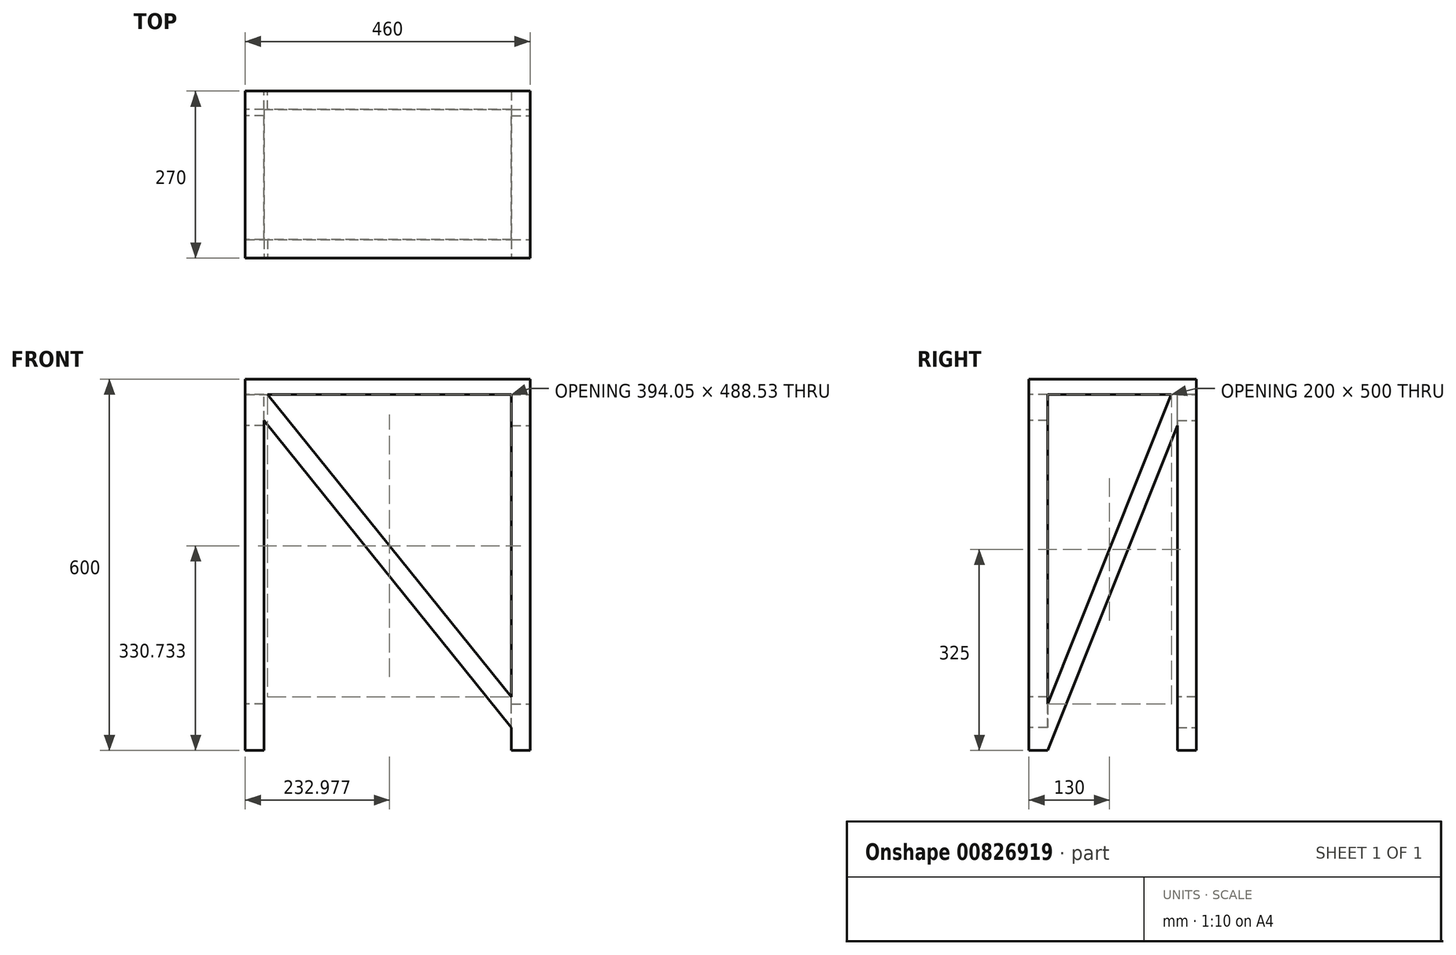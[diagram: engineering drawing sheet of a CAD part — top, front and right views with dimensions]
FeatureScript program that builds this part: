
annotation { "Feature Type Name" : "Feature", "Feature Type Description" : "" }
export const myFeature = defineFeature(function(context is Context, id is Id, definition is map)
    precondition{}
    {
        {
            var Q0;
            Q0=qCreatedBy(makeId("Top.planeOp"),FACE);
            var sketch = newSketch(context, id + "F0", { "sketchPlane" : qUnion([Q0])});
            skLineSegment(sketch, "E0.bottom", {"start": v(-200, 105) * mm, "end": v(-230, 105) * mm});
            skLineSegment(sketch, "E0.top", {"start": v(-200, 135) * mm, "end": v(-230, 135) * mm});
            skLineSegment(sketch, "E0.left", {"start": v(-200, 105) * mm, "end": v(-200, 135) * mm});
            skLineSegment(sketch, "E0.right", {"start": v(-230, 105) * mm, "end": v(-230, 135) * mm});
            skPoint(sketch, "E0.middle", {"position": v(-215, 120) * mm});
            skLineSegment(sketch, "E1.0.1.0", {"start": v(-200, -135) * mm, "end": v(-200, -105) * mm});
            skLineSegment(sketch, "E1.0.1.1", {"start": v(-230, -135) * mm, "end": v(-230, -105) * mm});
            skLineSegment(sketch, "E1.0.1.2", {"start": v(-200, -135) * mm, "end": v(-230, -135) * mm});
            skLineSegment(sketch, "E1.0.1.3", {"start": v(-200, -105) * mm, "end": v(-230, -105) * mm});
            skPoint(sketch, "E1.0.1.4", {"position": v(-215, -120) * mm});
            skLineSegment(sketch, "E1.1.0.0", {"start": v(230, 105) * mm, "end": v(230, 135) * mm});
            skLineSegment(sketch, "E1.1.0.1", {"start": v(200, 105) * mm, "end": v(200, 135) * mm});
            skLineSegment(sketch, "E1.1.0.2", {"start": v(230, 105) * mm, "end": v(200, 105) * mm});
            skLineSegment(sketch, "E1.1.0.3", {"start": v(230, 135) * mm, "end": v(200, 135) * mm});
            skPoint(sketch, "E1.1.0.4", {"position": v(215, 120) * mm});
            skLineSegment(sketch, "E1.1.1.0", {"start": v(230, -135) * mm, "end": v(230, -105) * mm});
            skLineSegment(sketch, "E1.1.1.1", {"start": v(200, -135) * mm, "end": v(200, -105) * mm});
            skLineSegment(sketch, "E1.1.1.2", {"start": v(230, -135) * mm, "end": v(200, -135) * mm});
            skLineSegment(sketch, "E1.1.1.3", {"start": v(230, -105) * mm, "end": v(200, -105) * mm});
            skPoint(sketch, "E1.1.1.4", {"position": v(215, -120) * mm});
            skLineSegment(sketch, "E1.direction1", {"start": v(-230, 105) * mm, "end": v(200, 105) * mm, "construction": true});
            skLineSegment(sketch, "E1.direction2", {"start": v(-230, 105) * mm, "end": v(-230, -135) * mm, "construction": true});
            skSolve(sketch);
        }
        {
            var Q0;
            Q0 = qSketchRegion(id + "F0", true);
            extrude(context, id + "F1", {"entities" : qUnion([Q0]), "oppositeDirection" : true, "depth" : 600 * mm, "offsetDistance" : 25 * mm});
        }
        {
            var Q0;
            Q0=makeQuery(id+"F1.opExtrude","CAP_FACE",FACE,{"disambiguationData":[OSD([sQuery(id+"F0.wireOp",EDGE,"E0.bottom"),sQuery(id+"F0.wireOp",EDGE,"E0.top"),sQuery(id+"F0.wireOp",EDGE,"E0.left"),sQuery(id+"F0.wireOp",EDGE,"E0.right")])],"isStart":true});
            var sketch = newSketch(context, id + "F2", { "sketchPlane" : qUnion([Q0])});
            skLineSegment(sketch, "E2.bottom", {"start": v(-230, 135) * mm, "end": v(230, 135) * mm});
            skLineSegment(sketch, "E2.top", {"start": v(-230, -135) * mm, "end": v(230, -135) * mm});
            skLineSegment(sketch, "E2.left", {"start": v(-230, 135) * mm, "end": v(-230, -135) * mm});
            skLineSegment(sketch, "E2.right", {"start": v(230, 135) * mm, "end": v(230, -135) * mm});
            skSolve(sketch);
        }
        {
            var Q0;
            Q0 = qSketchRegion(id + "F2", true);
            extrude(context, id + "F3", {"entities" : qUnion([Q0]), "operationType" : NewBodyOperationType.ADD, "oppositeDirection" : true, "depth" : 25 * mm, "offsetDistance" : 25 * mm});
        }
        {
            var Q0;
            Q0=makeQuery(id+"F3.boolean.opBoolean","MERGE",FACE,{"derivedFrom":[makeQuery(id+"F1.opExtrude","SWEPT_FACE",FACE,{"disambiguationData":[OSD([sQuery(id+"F0.wireOp",EDGE,"E1.0.1.2")])]}),makeQuery(id+"F1.opExtrude","SWEPT_FACE",FACE,{"disambiguationData":[OSD([sQuery(id+"F0.wireOp",EDGE,"E1.1.1.2")])]}),makeQuery(id+"F3.opExtrude","SWEPT_FACE",FACE,{"disambiguationData":[OSD([sQuery(id+"F2.wireOp",EDGE,"E2.top")])]})]});
            var sketch = newSketch(context, id + "F4", { "sketchPlane" : qUnion([Q0])});
            skLineSegment(sketch, "E3", {"start": v(-230, -29.7) * mm, "end": v(230, -600) * mm});
            skLineSegment(sketch, "E4", {"start": v(230, -600) * mm, "end": v(230, -550.73) * mm});
            skLineSegment(sketch, "E5", {"start": v(230, -550.73) * mm, "end": v(-214.2, 0) * mm});
            skLineSegment(sketch, "E6", {"start": v(-214.2, 0) * mm, "end": v(-230, -29.7) * mm});
            skSolve(sketch);
        }
        {
            var Q0;
            {var subQ3=sQuery(id+"F4.wireOp",EDGE,"E5");var subQ5=makeQuery(id+"F3.opExtrude","CAP_EDGE",EDGE,{"disambiguationData":[OSD([sQuery(id+"F2.wireOp",EDGE,"E2.top")])],"isStart":false});var subQ9=makeQuery(id+"F4.imprint","INTERSECT",VERTEX,{"derivedFrom":[subQ5,subQ3]});Q0=makeQuery(id+"F4.imprint","IMPRINT",FACE,{"disambiguationData":[TD([[makeQuery(id+"F4.imprint","IMPRINT",EDGE,{"disambiguationData":[TD([[subQ9,1.0]])],"derivedFrom":subQ3}),1.0]])]});}
            extrude(context, id + "F5", {"entities" : qUnion([Q0]), "operationType" : NewBodyOperationType.ADD, "oppositeDirection" : true, "depth" : 30 * mm, "offsetDistance" : 25 * mm});
        }
        {
            var Q0;
            Q0=makeQuery(id+"F1.opExtrude","SWEPT_FACE",FACE,{"disambiguationData":[OSD([sQuery(id+"F0.wireOp",EDGE,"E0.bottom")])]});
            var sketch = newSketch(context, id + "F6", { "sketchPlane" : qUnion([Q0])});
            skLineSegment(sketch, "E7.0", {"start": v(-230, -29.7) * mm, "end": v(230, -600) * mm});
            skLineSegment(sketch, "E8.0", {"start": v(230, -550.73) * mm, "end": v(-214.2, 0) * mm});
            skLineSegment(sketch, "E9.0", {"start": v(-214.2, 0) * mm, "end": v(-230, -29.7) * mm});
            skLineSegment(sketch, "E10.0", {"start": v(230, -600) * mm, "end": v(230, -550.73) * mm});
            skSolve(sketch);
        }
        {
            var Q0;
            Q0 = qSketchRegion(id + "F6", true);
            extrude(context, id + "F7", {"entities" : qUnion([Q0]), "operationType" : NewBodyOperationType.ADD, "oppositeDirection" : true, "depth" : 30 * mm, "offsetDistance" : 25 * mm});
        }
        {
            var Q0;
            Q0=makeQuery(id+"F3.boolean.opBoolean","MERGE",FACE,{"derivedFrom":[makeQuery(id+"F1.opExtrude","SWEPT_FACE",FACE,{"disambiguationData":[OSD([sQuery(id+"F0.wireOp",EDGE,"E0.right")])]}),makeQuery(id+"F1.opExtrude","SWEPT_FACE",FACE,{"disambiguationData":[OSD([sQuery(id+"F0.wireOp",EDGE,"E1.0.1.1")])]}),makeQuery(id+"F3.opExtrude","SWEPT_FACE",FACE,{"disambiguationData":[OSD([sQuery(id+"F2.wireOp",EDGE,"E2.left")])]})]});
            var sketch = newSketch(context, id + "F8", { "sketchPlane" : qUnion([Q0])});
            skLineSegment(sketch, "E11", {"start": v(-135, 0) * mm, "end": v(105, -600) * mm});
            skLineSegment(sketch, "E12", {"start": v(105, -600) * mm, "end": v(135, -600) * mm});
            skLineSegment(sketch, "E13", {"start": v(135, -600) * mm, "end": v(-105, 0) * mm});
            skLineSegment(sketch, "E14", {"start": v(-105, 0) * mm, "end": v(-135, 0) * mm});
            skSolve(sketch);
        }
        {
            var Q0;
            {var subQ1=makeQuery(id+"F3.opExtrude","CAP_EDGE",EDGE,{"disambiguationData":[OSD([sQuery(id+"F2.wireOp",EDGE,"E2.left")])],"isStart":false});var subQ3=sQuery(id+"F8.wireOp",EDGE,"E13");var subQ4=makeQuery(id+"F8.imprint","INTERSECT",VERTEX,{"derivedFrom":[subQ1,subQ3]});Q0=makeQuery(id+"F8.imprint","IMPRINT",FACE,{"disambiguationData":[TD([[makeQuery(id+"F8.imprint","IMPRINT",EDGE,{"disambiguationData":[TD([[subQ4,1.0]])],"derivedFrom":subQ3}),1.0]])]});}
            extrude(context, id + "F9", {"entities" : qUnion([Q0]), "operationType" : NewBodyOperationType.ADD, "oppositeDirection" : true, "depth" : 30 * mm, "offsetDistance" : 25 * mm});
        }
        {
            var Q0;
            Q0=makeQuery(id+"F3.boolean.opBoolean","MERGE",FACE,{"derivedFrom":[makeQuery(id+"F1.opExtrude","SWEPT_FACE",FACE,{"disambiguationData":[OSD([sQuery(id+"F0.wireOp",EDGE,"E1.1.0.0")])]}),makeQuery(id+"F1.opExtrude","SWEPT_FACE",FACE,{"disambiguationData":[OSD([sQuery(id+"F0.wireOp",EDGE,"E1.1.1.0")])]}),makeQuery(id+"F3.opExtrude","SWEPT_FACE",FACE,{"disambiguationData":[OSD([sQuery(id+"F2.wireOp",EDGE,"E2.right")])]})]});
            var sketch = newSketch(context, id + "F10", { "sketchPlane" : qUnion([Q0])});
            skLineSegment(sketch, "E15.0", {"start": v(-105, -525) * mm, "end": v(95, -25) * mm});
            skLineSegment(sketch, "E16.0", {"start": v(105, -75) * mm, "end": v(-105, -600) * mm});
            skLineSegment(sketch, "E17.0", {"start": v(105, -75) * mm, "end": v(105, -25) * mm});
            skLineSegment(sketch, "E18.0", {"start": v(105, -25) * mm, "end": v(95, -25) * mm});
            skLineSegment(sketch, "E19.0", {"start": v(-105, -600) * mm, "end": v(-105, -525) * mm});
            skPoint(sketch, "E20.orphan", {"position": v(-105, -25) * mm});
            skPoint(sketch, "E21.orphan", {"position": v(105, -600) * mm});
            skSolve(sketch);
        }
        {
            var Q0;
            Q0=makeQuery(id+"F10.imprint","IMPRINT",FACE,{"disambiguationData":[TD([[makeQuery(id+"F10.imprint","IMPRINT",EDGE,{"derivedFrom":sQuery(id+"F10.wireOp",EDGE,"E15.0")}),-1.0]])]});
            extrude(context, id + "F11", {"entities" : qUnion([Q0]), "operationType" : NewBodyOperationType.ADD, "oppositeDirection" : true, "depth" : 30 * mm, "offsetDistance" : 25 * mm});
        }
    });
